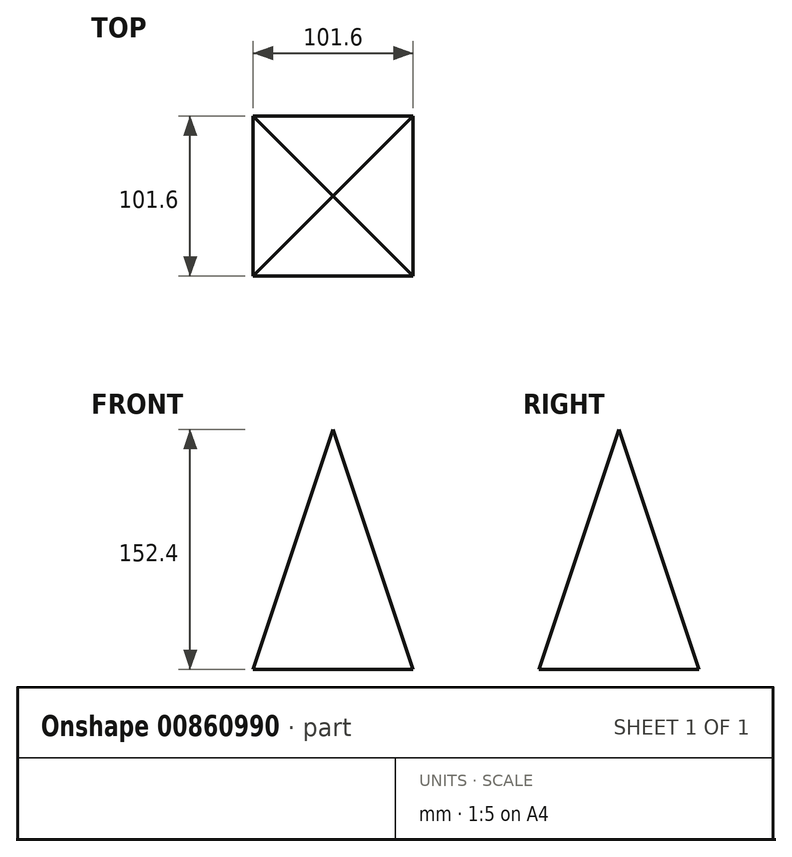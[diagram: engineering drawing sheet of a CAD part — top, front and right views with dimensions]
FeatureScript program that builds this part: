
annotation { "Feature Type Name" : "Feature", "Feature Type Description" : "" }
export const myFeature = defineFeature(function(context is Context, id is Id, definition is map)
    precondition{}
    {
        {
            var Q0;
            Q0=qCreatedBy(makeId("Top.planeOp"),FACE);
            var sketch = newSketch(context, id + "F0", { "sketchPlane" : qUnion([Q0])});
            skLineSegment(sketch, "E0.bottom", {"start": v(50.8, -50.8) * mm, "end": v(-50.8, -50.8) * mm});
            skLineSegment(sketch, "E0.top", {"start": v(50.8, 50.8) * mm, "end": v(-50.8, 50.8) * mm});
            skLineSegment(sketch, "E0.left", {"start": v(50.8, -50.8) * mm, "end": v(50.8, 50.8) * mm});
            skLineSegment(sketch, "E0.right", {"start": v(-50.8, -50.8) * mm, "end": v(-50.8, 50.8) * mm});
            skSolve(sketch);
        }
        {
            var Q0;
            Q0=qCreatedBy(makeId("Top.planeOp"),FACE);
            cPlane(context, id + "F1", {"entities" : qUnion([Q0]), "cplaneType" : CPlaneType.OFFSET, "offset" : 152.4 * mm, "width" : 152.4 * mm, "height" : 152.4 * mm});
        }
        {
            var Q0;
            Q0=qCreatedBy(id+"F1.planeOp",FACE);
            var sketch = newSketch(context, id + "F2", { "sketchPlane" : qUnion([Q0])});
            skPoint(sketch, "E1", {"position": v(0, 0) * mm});
            skSolve(sketch);
        }
        {
            var Q0;
            Q0=makeQuery(id+"F0.imprint","IMPRINT",FACE,{"disambiguationData":[TD([[makeQuery(id+"F0.imprint","IMPRINT",EDGE,{"derivedFrom":sQuery(id+"F0.wireOp",EDGE,"E0.bottom")}),-1.0]])]});
            var Q1;
            Q1=sQuery(id+"F2.wireOp",VERTEX,"E1");
            loft(context, id + "F3", {"sheetProfilesArray" : [{ "sheetProfileEntities" : qUnion([Q0]) }, { "sheetProfileEntities" : qUnion([Q1]) }]});
        }
    });
